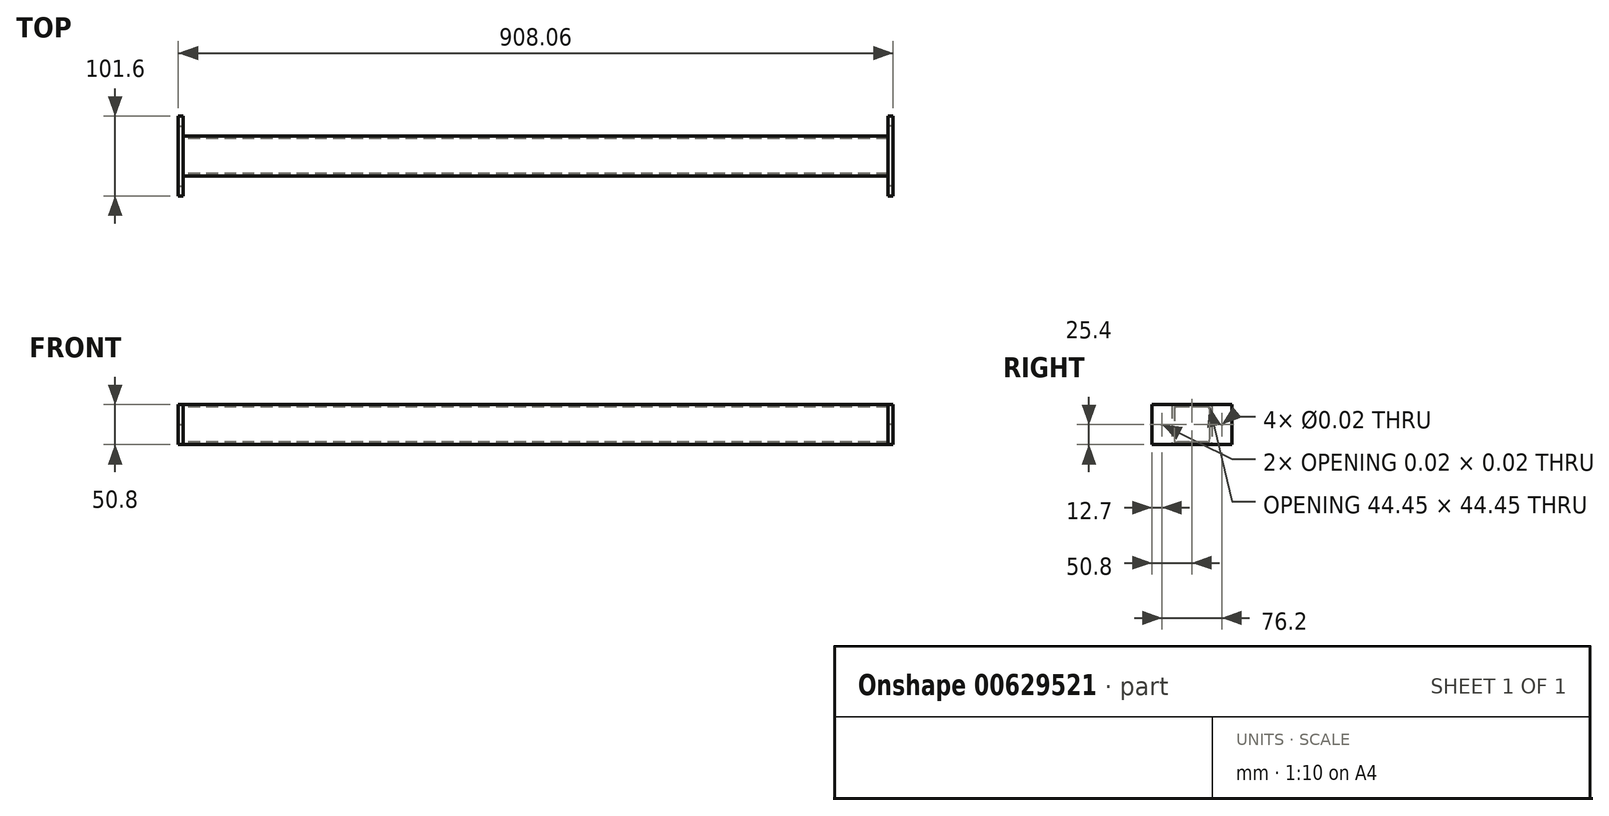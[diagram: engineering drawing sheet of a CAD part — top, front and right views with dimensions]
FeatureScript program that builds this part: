
annotation { "Feature Type Name" : "Feature", "Feature Type Description" : "" }
export const myFeature = defineFeature(function(context is Context, id is Id, definition is map)
    precondition{}
    {
        {
            var Q0;
            Q0=qCreatedBy(makeId("Right.planeOp"),FACE);
            var sketch = newSketch(context, id + "F0", { "sketchPlane" : qUnion([Q0])});
            skLineSegment(sketch, "E0.bottom", {"start": v(22.86, 25.4) * mm, "end": v(-22.86, 25.4) * mm});
            skLineSegment(sketch, "E0.top", {"start": v(22.86, -25.4) * mm, "end": v(-22.86, -25.4) * mm});
            skLineSegment(sketch, "E0.left", {"start": v(25.4, 22.86) * mm, "end": v(25.4, -22.86) * mm});
            skLineSegment(sketch, "E0.right", {"start": v(-25.4, 22.86) * mm, "end": v(-25.4, -22.86) * mm});
            skPoint(sketch, "E0.middle", {"position": v(0, 0) * mm});
            skLineSegment(sketch, "E1.bottom", {"start": v(19.69, 22.23) * mm, "end": v(-19.68, 22.23) * mm});
            skLineSegment(sketch, "E1.top", {"start": v(19.69, -22.23) * mm, "end": v(-19.69, -22.23) * mm});
            skLineSegment(sketch, "E1.left", {"start": v(22.23, 19.69) * mm, "end": v(22.23, -19.69) * mm});
            skLineSegment(sketch, "E1.right", {"start": v(-22.23, 19.69) * mm, "end": v(-22.23, -19.69) * mm});
            skPoint(sketch, "E2.visualSharp", {"position": v(-25.4, 25.4) * mm});
            skArc(sketch, "E2.filletArc", {"start": v(-22.86, 25.4) * mm, "mid": v(-24.66, 24.66) * mm, "end": v(-25.4, 22.86) * mm});
            skPoint(sketch, "E3.visualSharp", {"position": v(25.4, 25.4) * mm});
            skArc(sketch, "E3.filletArc", {"start": v(25.4, 22.86) * mm, "mid": v(24.66, 24.66) * mm, "end": v(22.86, 25.4) * mm});
            skPoint(sketch, "E4.visualSharp", {"position": v(22.23, 22.23) * mm});
            skArc(sketch, "E4.filletArc", {"start": v(22.23, 19.69) * mm, "mid": v(21.48, 21.48) * mm, "end": v(19.69, 22.23) * mm});
            skPoint(sketch, "E5.visualSharp", {"position": v(22.22, -22.23) * mm});
            skArc(sketch, "E5.filletArc", {"start": v(19.69, -22.23) * mm, "mid": v(21.48, -21.48) * mm, "end": v(22.23, -19.69) * mm});
            skPoint(sketch, "E6.visualSharp", {"position": v(25.4, -25.4) * mm});
            skArc(sketch, "E6.filletArc", {"start": v(22.86, -25.4) * mm, "mid": v(24.66, -24.66) * mm, "end": v(25.4, -22.86) * mm});
            skPoint(sketch, "E7.visualSharp", {"position": v(-25.4, -25.4) * mm});
            skArc(sketch, "E7.filletArc", {"start": v(-25.4, -22.86) * mm, "mid": v(-24.66, -24.66) * mm, "end": v(-22.86, -25.4) * mm});
            skPoint(sketch, "E8.visualSharp", {"position": v(-22.23, -22.23) * mm});
            skArc(sketch, "E8.filletArc", {"start": v(-22.23, -19.69) * mm, "mid": v(-21.48, -21.48) * mm, "end": v(-19.69, -22.23) * mm});
            skPoint(sketch, "E9.visualSharp", {"position": v(-22.22, 22.23) * mm});
            skArc(sketch, "E9.filletArc", {"start": v(-19.68, 22.23) * mm, "mid": v(-21.48, 21.48) * mm, "end": v(-22.22, 19.69) * mm});
            skSolve(sketch);
        }
        {
            var Q0;
            Q0=qSketchRegion(id+"F0",true);
            extrude(context, id + "F1", {"entities" : qUnion([Q0]), "depth" : 895.35 * mm, "symmetric" : true});
        }
        {
            var Q0;
            Q0=makeQuery(id+"F1.opExtrude","CAP_FACE",FACE,{"disambiguationData":[OSD([sQuery(id+"F0.wireOp",EDGE,"E0.bottom"),sQuery(id+"F0.wireOp",EDGE,"E0.top"),sQuery(id+"F0.wireOp",EDGE,"E0.left"),sQuery(id+"F0.wireOp",EDGE,"E0.right"),sQuery(id+"F0.wireOp",EDGE,"E1.bottom"),sQuery(id+"F0.wireOp",EDGE,"E1.top"),sQuery(id+"F0.wireOp",EDGE,"E1.left"),sQuery(id+"F0.wireOp",EDGE,"E1.right"),sQuery(id+"F0.wireOp",EDGE,"E2.filletArc"),sQuery(id+"F0.wireOp",EDGE,"E3.filletArc"),sQuery(id+"F0.wireOp",EDGE,"E4.filletArc"),sQuery(id+"F0.wireOp",EDGE,"E5.filletArc"),sQuery(id+"F0.wireOp",EDGE,"E6.filletArc"),sQuery(id+"F0.wireOp",EDGE,"E7.filletArc"),sQuery(id+"F0.wireOp",EDGE,"E8.filletArc"),sQuery(id+"F0.wireOp",EDGE,"E9.filletArc")])],"isStart":false});
            var sketch = newSketch(context, id + "F2", { "sketchPlane" : qUnion([Q0])});
            skLineSegment(sketch, "E10.bottom", {"start": v(50.8, 25.4) * mm, "end": v(-50.8, 25.4) * mm});
            skLineSegment(sketch, "E10.top", {"start": v(50.8, -25.4) * mm, "end": v(-50.8, -25.4) * mm});
            skLineSegment(sketch, "E10.left", {"start": v(50.8, 25.4) * mm, "end": v(50.8, -25.4) * mm});
            skLineSegment(sketch, "E10.right", {"start": v(-50.8, 25.4) * mm, "end": v(-50.8, -25.4) * mm});
            skPoint(sketch, "E10.middle", {"position": v(0, 0) * mm});
            skSolve(sketch);
        }
        {
            var Q0;
            Q0=qSketchRegion(id+"F2",true);
            extrude(context, id + "F3", {"entities" : qUnion([Q0]), "depth" : 6.35 * mm});
        }
        {
            var Q0;
            Q0=makeQuery(id+"F3.opExtrude","CAP_FACE",FACE,{"disambiguationData":[OSD([sQuery(id+"F2.wireOp",EDGE,"E10.bottom"),sQuery(id+"F2.wireOp",EDGE,"E10.top"),sQuery(id+"F2.wireOp",EDGE,"E10.left"),sQuery(id+"F2.wireOp",EDGE,"E10.right")])],"isStart":false});
            var sketch = newSketch(context, id + "F4", { "sketchPlane" : qUnion([Q0])});
            skLineSegment(sketch, "E11", {"start": v(-38.1, 0) * mm, "end": v(38.1, 0) * mm, "construction": true});
            skSolve(sketch);
        }
        {
            var Q0;
            Q0=sQuery(id+"F4.wireOp",VERTEX,"E11.start");
            var Q1;
            Q1=sQuery(id+"F4.wireOp",VERTEX,"E11.end");
            var Q2;
            Q2=makeQuery(id+"F3.opExtrude","SWEPT_BODY",BODY,{"disambiguationData":[OSD([sQuery(id+"F2.wireOp",EDGE,"E10.bottom"),sQuery(id+"F2.wireOp",EDGE,"E10.top"),sQuery(id+"F2.wireOp",EDGE,"E10.left"),sQuery(id+"F2.wireOp",EDGE,"E10.right")])]});
            hole(context, id + "F5", {"style" : HoleStyle.SIMPLE, "endStyle" : HoleEndStyle.THROUGH, "standardTappedOrClearance" : lookupTablePath({ "standard" : "ANSI", "size" : "13/32 (0.4)", "type" : "Drilled" }), "standardBlindInLast" : lookupTablePath({ "standard" : "ANSI", "size" : "13/32", "type" : "Drilled" }), "holeDiameter" : 13 / 812.8 * mm, "isTappedThrough" : true, "tappedDepth" : 12.7 * mm, "tapClearance" : 3, "locations" : qUnion([Q0, Q1]), "scope" : qUnion([Q2])});
        }
        {
            var Q0;
            Q0=makeQuery(id+"F3.opExtrude","SWEPT_BODY",BODY,{"disambiguationData":[OSD([sQuery(id+"F2.wireOp",EDGE,"E10.bottom"),sQuery(id+"F2.wireOp",EDGE,"E10.top"),sQuery(id+"F2.wireOp",EDGE,"E10.left"),sQuery(id+"F2.wireOp",EDGE,"E10.right")])]});
            var Q1;
            Q1=qCreatedBy(makeId("Right.planeOp"),FACE);
            mirror(context, id + "F6", {"entities" : qUnion([Q0]), "mirrorPlane" : qUnion([Q1])});
        }
    });
